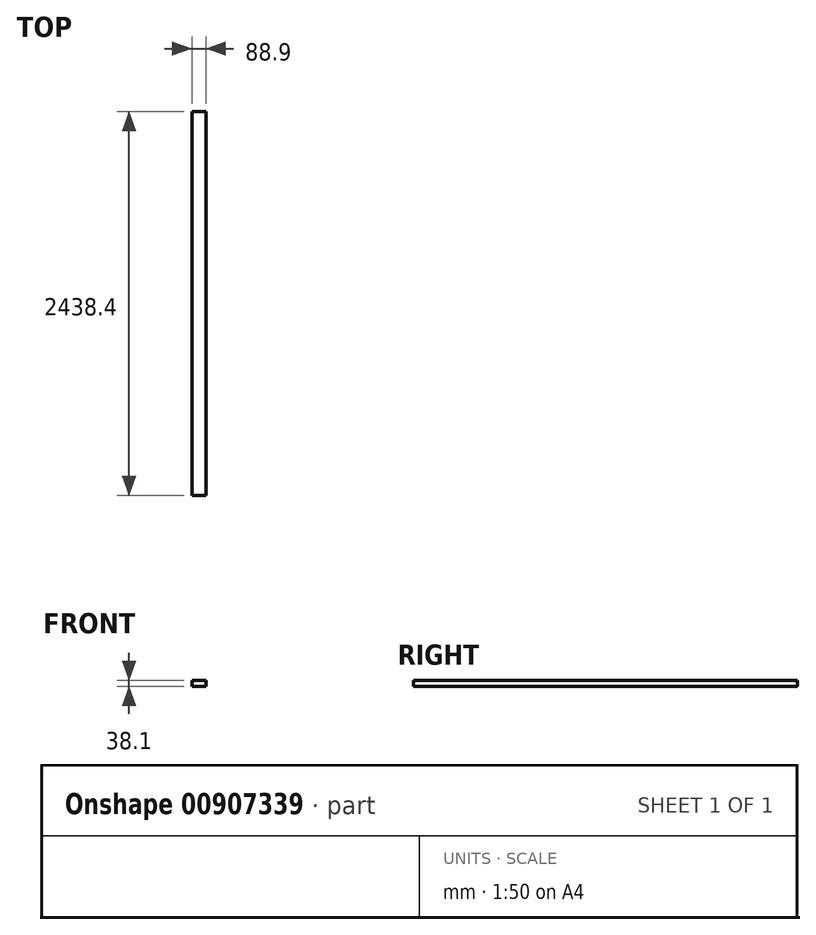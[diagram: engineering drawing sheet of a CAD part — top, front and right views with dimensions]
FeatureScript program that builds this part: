
annotation { "Feature Type Name" : "Feature", "Feature Type Description" : "" }
export const myFeature = defineFeature(function(context is Context, id is Id, definition is map)
    precondition{}
    {
        {
            var Q0;
            Q0=qCreatedBy(makeId("Front.planeOp"),FACE);
            var sketch = newSketch(context, id + "F0", { "sketchPlane" : qUnion([Q0])});
            skLineSegment(sketch, "E0.bottom", {"start": v(-44.45, 19.05) * mm, "end": v(44.45, 19.05) * mm});
            skLineSegment(sketch, "E0.top", {"start": v(-44.45, -19.05) * mm, "end": v(44.45, -19.05) * mm});
            skLineSegment(sketch, "E0.left", {"start": v(-44.45, 19.05) * mm, "end": v(-44.45, -19.05) * mm});
            skLineSegment(sketch, "E0.right", {"start": v(44.45, 19.05) * mm, "end": v(44.45, -19.05) * mm});
            skPoint(sketch, "E0.middle", {"position": v(0, 0) * mm});
            skSolve(sketch);
        }
        {
            var Q0;
            Q0=makeQuery(id+"F0.imprint","IMPRINT",FACE,{"disambiguationData":[TD([[makeQuery(id+"F0.imprint","IMPRINT",EDGE,{"derivedFrom":sQuery(id+"F0.wireOp",EDGE,"E0.bottom")}),-1.0]])]});
            extrude(context, id + "F1", {"entities" : qUnion([Q0]), "endBound" : BoundingType.SYMMETRIC, "depth" : 2438.4 * mm, "offsetDistance" : 25.4 * mm});
        }
    });
